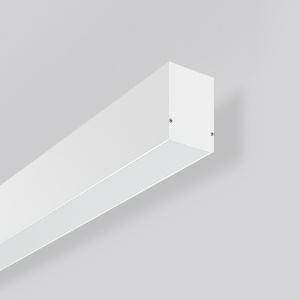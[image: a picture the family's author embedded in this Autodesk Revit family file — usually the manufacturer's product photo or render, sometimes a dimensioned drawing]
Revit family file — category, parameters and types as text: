
# Revit family: less_is_more_50_312613_002_1_76_a93b
name_source: partatom
category: Lighting Fixtures
units: mm (PartAtom-declared; Revit-internal decimal feet)

## family parameters
Cut with Voids When Loaded = No
Host = Face
Light Source = No
Part Type = Normal
Room Calculation Point = No
Round Connector Dimension = Use Diameter
Shared = No

## types (1)
- LESS IS MORE 50 (1 x LED Modul 840, 2650 lm, 4000)
    Apparent Load = 20 VA
    CIE Flux Codes = 48 80 96 100 100
    Color Rendering = 80
    Color Temperature = 4000
    Default Elevation = 1800 mm
    Description = Series: LESS IS MORE 50
Linear wall luminaires. Housing: extruded aluminium profile, powder-coated. End cap aluminium powder-coated. Diffuser made of non-yellowing plastic (PMMA), opal. Direct light emission. Suitable for Wall (surface). LED unit with integrated converter interchangeable and removable. Suitable for through-wiring. With sensors or as a safety luminaire on request. 
Colour: traffic white, matt (RAL 9016)
Length: 1967 mm
Width: 67 mm
Height: 75 mm
Lamp: LED
Socket: without socket
Colour temperature: 4000K
Colour rendering index (CRI): 80
System power: 20 W
Rated luminous flux: 2650 lm
Luminous efficiency: 133 lm/W
Control gear: Converter, dimmable, DALI
Protection class: I
Type of protection: IP 20
    Height = 75 mm
    Lamp = 1 x LED Modul 840
    Lamp Light Flux = 2650 lm
    Lamp count = 1
    Length = 1967 mm
    Lifetime = 50000 h
    Luminous efficacy = 133 lm/W
    Manufacturer = RZB
    ModVariant = No
    Model = 312613.002.1.76
    Mounting Place = Wall
    Mounting Type = Surface mounted
    Number of Poles = 1
    OnlyDefault = Yes
    Power Factor = 1
    Product Name = LESS IS MORE 50
    Product group = Surface mounted LED linear luminaires
    ProductGroupID = 2007
    Protection Class = Protection class I
    Protection Degree = IP 20
    RLX_Detail_Level = 1
    RLX_Emergency_Light_Flux = 0 lm
    RLX_Emergency_Type = 0
    RLX_Emergency_Type_DB = No
    RlxData = <blob elided: 35165 chars, md5=401b3f12>
    Socket = socket
    Standby Power = 0 W
    System Light Flux = 2650 lm
    System Power = 20 W
    Type Comments = Product without accessories
    Type Image = 312606.002.jpg
    URL = http://relux.com
    VarID = ---
    Voltage = 0 V
    Weight = 0.00 kg
    Width = 67 mm

## geometry (parser evidence)
native form markers: Blend x4, Sweep x9
no freeform markers — native parametric forms only
